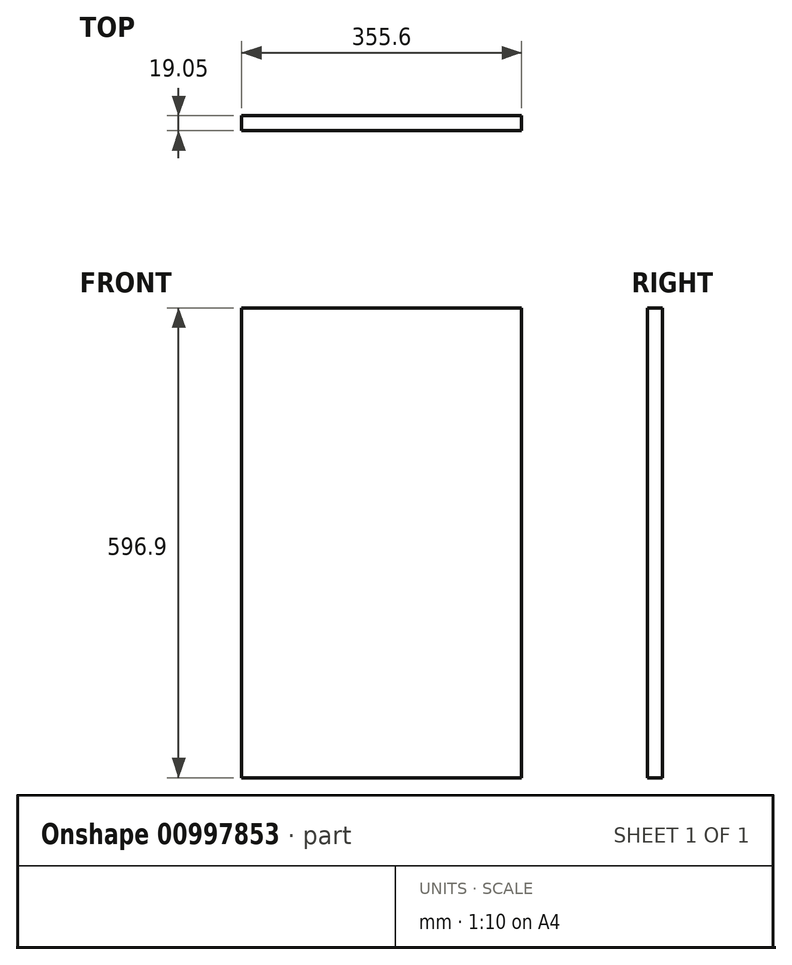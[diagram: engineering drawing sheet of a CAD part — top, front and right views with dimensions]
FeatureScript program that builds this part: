
annotation { "Feature Type Name" : "Feature", "Feature Type Description" : "" }
export const myFeature = defineFeature(function(context is Context, id is Id, definition is map)
    precondition{}
    {
        {
            var Q0;
            Q0=qCreatedBy(makeId("Front.planeOp"),FACE);
            var sketch = newSketch(context, id + "F0", { "sketchPlane" : qUnion([Q0])});
            skLineSegment(sketch, "E0.bottom", {"start": v(-177.8, 298.45) * mm, "end": v(177.8, 298.45) * mm});
            skLineSegment(sketch, "E0.top", {"start": v(-177.8, -298.45) * mm, "end": v(177.8, -298.45) * mm});
            skLineSegment(sketch, "E0.left", {"start": v(-177.8, 298.45) * mm, "end": v(-177.8, -298.45) * mm});
            skLineSegment(sketch, "E0.right", {"start": v(177.8, 298.45) * mm, "end": v(177.8, -298.45) * mm});
            skPoint(sketch, "E0.middle", {"position": v(0, 0) * mm});
            skSolve(sketch);
        }
        {
            var Q0;
            Q0=makeQuery(id+"F0.imprint","IMPRINT",FACE,{"disambiguationData":[TD([[makeQuery(id+"F0.imprint","IMPRINT",EDGE,{"derivedFrom":sQuery(id+"F0.wireOp",EDGE,"E0.bottom")}),-1.0]])]});
            extrude(context, id + "F1", {"entities" : qUnion([Q0]), "depth" : 19.05 * mm, "offsetDistance" : 25.4 * mm});
        }
    });
